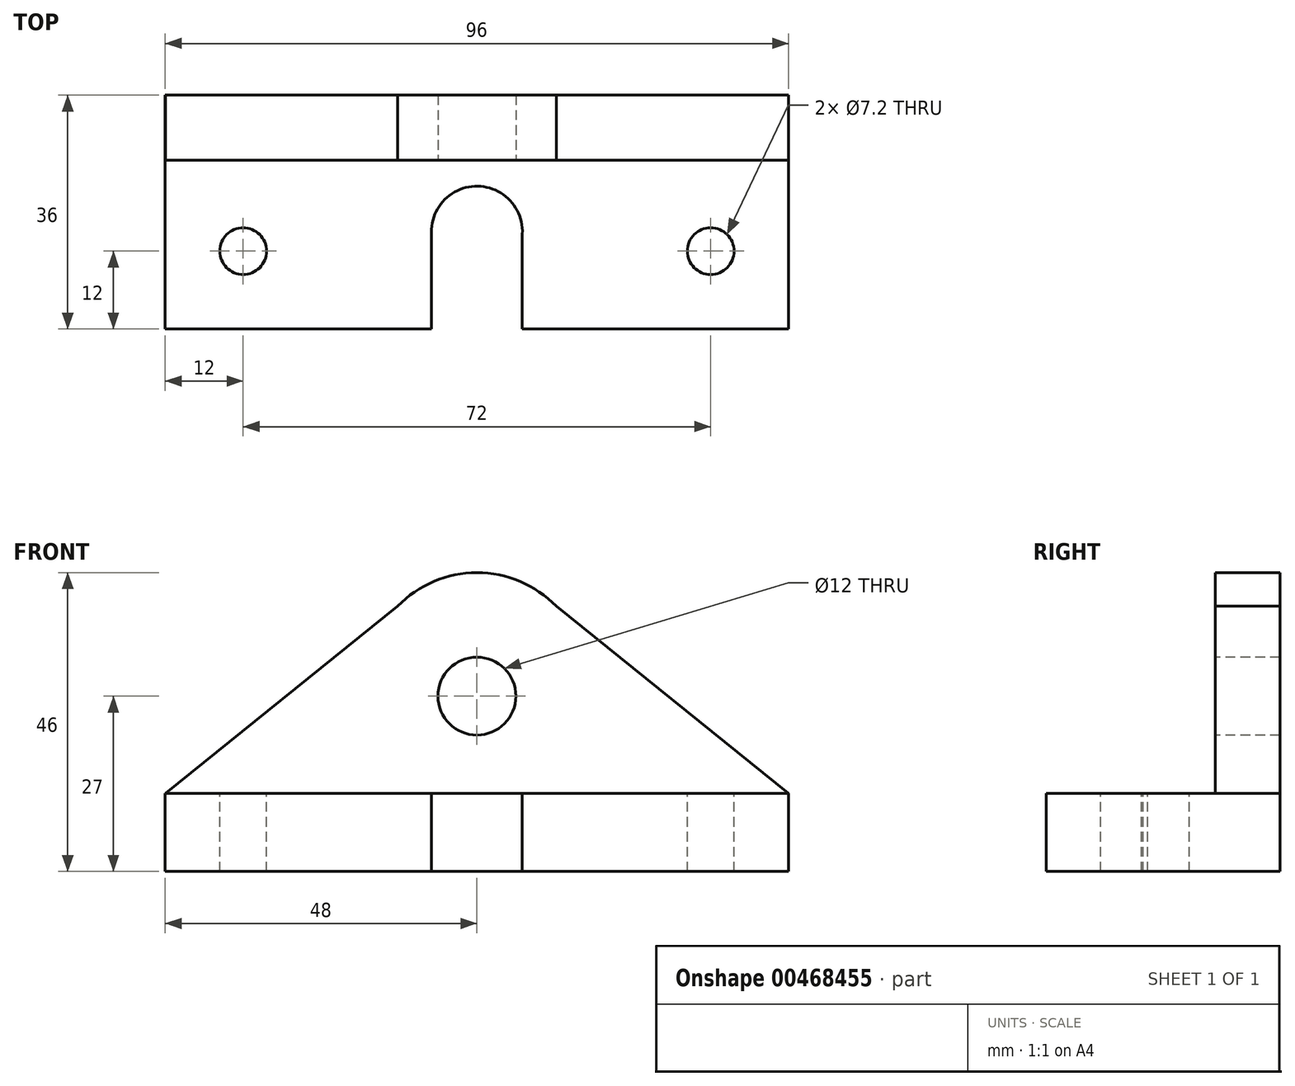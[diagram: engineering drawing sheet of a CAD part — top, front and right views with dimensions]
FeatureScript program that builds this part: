
annotation { "Feature Type Name" : "Feature", "Feature Type Description" : "" }
export const myFeature = defineFeature(function(context is Context, id is Id, definition is map)
    precondition{}
    {
        {
            var Q0;
            Q0=qCreatedBy(makeId("Top.planeOp"),FACE);
            var sketch = newSketch(context, id + "F0", { "sketchPlane" : qUnion([Q0])});
            skLineSegment(sketch, "E0.bottom", {"start": v(0, 0) * mm, "end": v(-96, 0) * mm});
            skLineSegment(sketch, "E0.top", {"start": v(0, 36) * mm, "end": v(-96, 36) * mm});
            skLineSegment(sketch, "E0.left", {"start": v(0, 0) * mm, "end": v(0, 36) * mm});
            skLineSegment(sketch, "E0.right", {"start": v(-96, 0) * mm, "end": v(-96, 36) * mm});
            skSolve(sketch);
        }
        {
            var Q0;
            Q0 = qSketchRegion(id + "F0", true);
            extrude(context, id + "F1", {"entities" : qUnion([Q0]), "depth" : 12 * mm});
        }
        {
            var Q0;
            Q0=makeQuery(id+"F1.opExtrude","CAP_FACE",FACE,{"disambiguationData":[OSD([sQuery(id+"F0.wireOp",EDGE,"E0.bottom"),sQuery(id+"F0.wireOp",EDGE,"E0.top"),sQuery(id+"F0.wireOp",EDGE,"E0.left"),sQuery(id+"F0.wireOp",EDGE,"E0.right")])],"isStart":false});
            var sketch = newSketch(context, id + "F2", { "sketchPlane" : qUnion([Q0])});
            skLineSegment(sketch, "E1", {"start": v(-48, 39.79) * mm, "end": v(-48, -7.7) * mm, "construction": true});
            skCircle(sketch, "E2", {"center": v(-12, 12) * mm, "radius": 3.6 * mm});
            skCircle(sketch, "E3.MirrorC", {"center": v(-84, 12) * mm, "radius": 3.6 * mm});
            skSolve(sketch);
        }
        {
            var Q0;
            Q0 = qSketchRegion(id + "F2", true);
            extrude(context, id + "F3", {"entities" : qUnion([Q0]), "operationType" : NewBodyOperationType.REMOVE, "endBound" : BoundingType.THROUGH_ALL, "oppositeDirection" : true, "depth" : 25 * mm});
        }
        {
            var Q0;
            Q0=makeQuery(id+"F1.opExtrude","CAP_FACE",FACE,{"disambiguationData":[OSD([sQuery(id+"F0.wireOp",EDGE,"E0.bottom"),sQuery(id+"F0.wireOp",EDGE,"E0.top"),sQuery(id+"F0.wireOp",EDGE,"E0.left"),sQuery(id+"F0.wireOp",EDGE,"E0.right")])],"isStart":false});
            var sketch = newSketch(context, id + "F4", { "sketchPlane" : qUnion([Q0])});
            skLineSegment(sketch, "E4", {"start": v(-48, 40.21) * mm, "end": v(-48, -8.58) * mm, "construction": true});
            skArc(sketch, "E5", {"start": v(-41, 14.65) * mm, "mid": v(-47.87, 22) * mm, "end": v(-55, 14.9) * mm});
            skLineSegment(sketch, "E6", {"start": v(-41, 14.65) * mm, "end": v(-41, -1.47) * mm});
            skLineSegment(sketch, "E7", {"start": v(-55, 14.9) * mm, "end": v(-55, -1.47) * mm});
            skLineSegment(sketch, "E8", {"start": v(-55, -1.47) * mm, "end": v(-41, -1.47) * mm});
            skSolve(sketch);
        }
        {
            var Q0;
            Q0 = qSketchRegion(id + "F4", true);
            extrude(context, id + "F5", {"entities" : qUnion([Q0]), "operationType" : NewBodyOperationType.REMOVE, "endBound" : BoundingType.THROUGH_ALL, "oppositeDirection" : true, "depth" : 25 * mm});
        }
        {
            var Q0;
            Q0=makeQuery(id+"F1.opExtrude","SWEPT_FACE",FACE,{"disambiguationData":[OSD([sQuery(id+"F0.wireOp",EDGE,"E0.top")])]});
            cPlane(context, id + "F6", {"entities" : qUnion([Q0]), "cplaneType" : CPlaneType.OFFSET, "offset" : 0 * mm, "oppositeDirection" : true, "width" : 150 * mm, "height" : 150 * mm});
        }
        {
            var Q0;
            Q0=qCreatedBy(id+"F6.planeOp",FACE);
            var sketch = newSketch(context, id + "F7", { "sketchPlane" : qUnion([Q0])});
            skLineSegment(sketch, "E9", {"start": v(0, 11.99) * mm, "end": v(96, 11.99) * mm});
            skLineSegment(sketch, "E10", {"start": v(48, 49.53) * mm, "end": v(48, 8.47) * mm, "construction": true});
            skArc(sketch, "E11", {"start": v(60.2, 40.84) * mm, "mid": v(48, 46) * mm, "end": v(35.8, 40.84) * mm});
            skLineSegment(sketch, "E12", {"start": v(35.8, 40.84) * mm, "end": v(0, 11.99) * mm});
            skLineSegment(sketch, "E13", {"start": v(60.2, 40.84) * mm, "end": v(96, 11.99) * mm});
            skPoint(sketch, "E14.start.orphan", {"position": v(0, 38.17) * mm});
            skPoint(sketch, "E15.center.orphan", {"position": v(48, 27) * mm});
            skSolve(sketch);
        }
        {
            var Q0;
            Q0 = qSketchRegion(id + "F7", true);
            extrude(context, id + "F8", {"entities" : qUnion([Q0]), "operationType" : NewBodyOperationType.ADD, "oppositeDirection" : true, "depth" : 10 * mm});
        }
        {
            var Q0;
            Q0=makeQuery(id+"F8.opExtrude","CAP_FACE",FACE,{"disambiguationData":[OSD([sQuery(id+"F7.wireOp",EDGE,"E9"),sQuery(id+"F7.wireOp",EDGE,"E11"),sQuery(id+"F7.wireOp",EDGE,"E12"),sQuery(id+"F7.wireOp",EDGE,"E13")])],"isStart":false});
            var sketch = newSketch(context, id + "F9", { "sketchPlane" : qUnion([Q0])});
            skCircle(sketch, "E16", {"center": v(-48, 27) * mm, "radius": 6 * mm});
            skSolve(sketch);
        }
        {
            var Q0;
            Q0=makeQuery(id+"F9.imprint","IMPRINT",FACE,{"disambiguationData":[TD([[makeQuery(id+"F9.imprint","IMPRINT",EDGE,{"derivedFrom":sQuery(id+"F9.wireOp",EDGE,"E16")}),1.0]])]});
            var Q1;
            Q1=sQuery(id+"F9.wireOp",EDGE,"E16");
            extrude(context, id + "F10", {"entities" : qUnion([Q0]), "operationType" : NewBodyOperationType.REMOVE, "surfaceEntities" : qUnion([Q1]), "endBound" : BoundingType.THROUGH_ALL, "oppositeDirection" : true, "depth" : 0 * mm});
        }
    });
